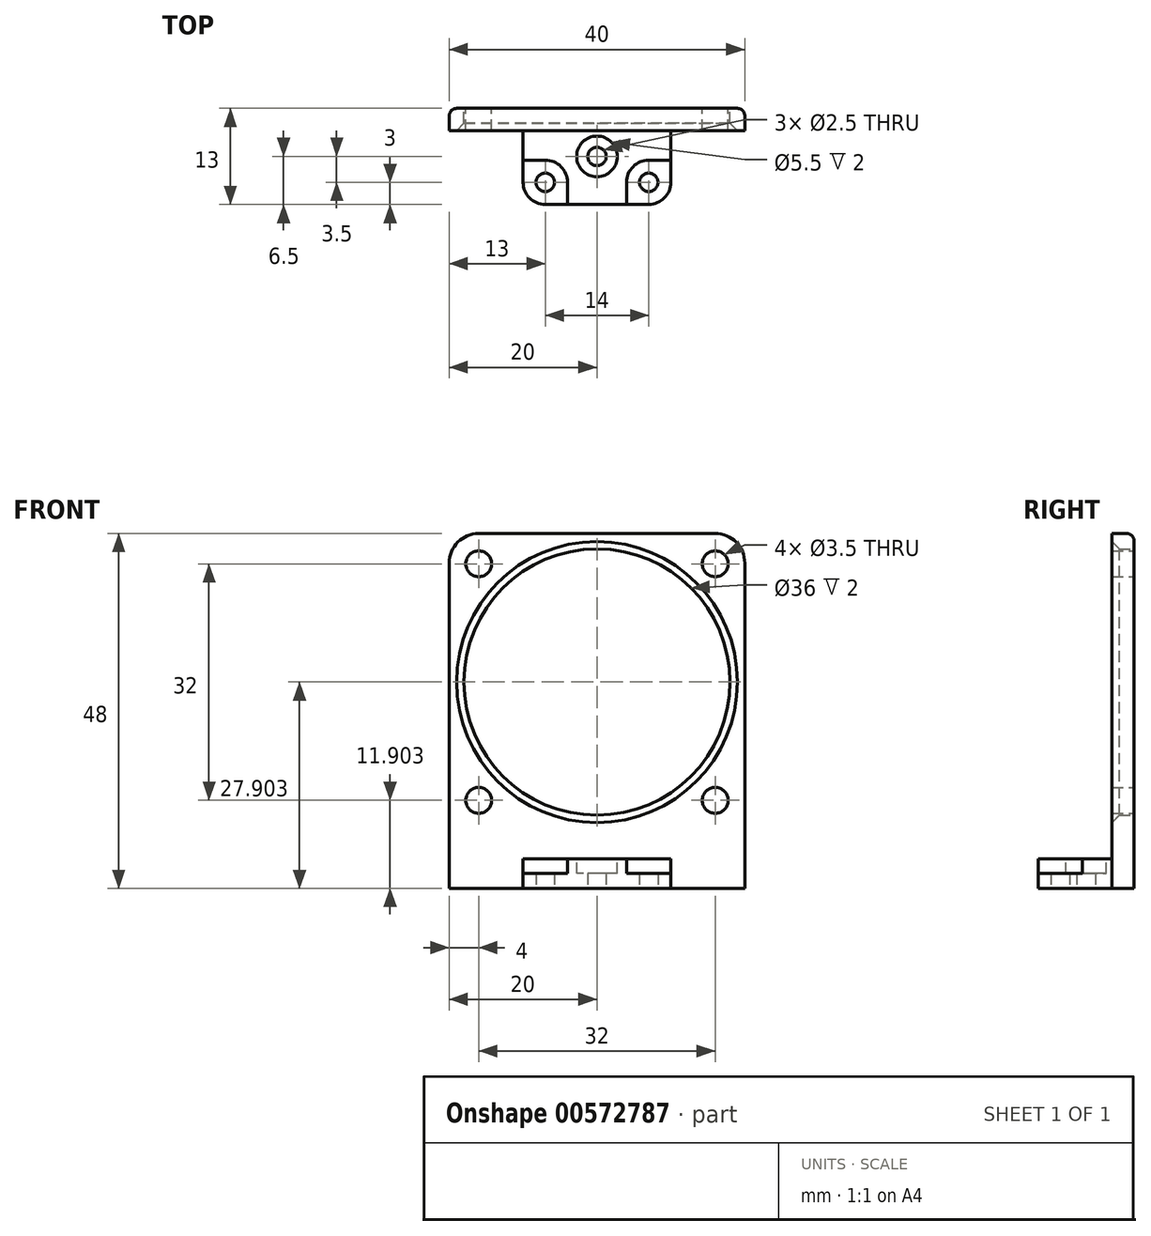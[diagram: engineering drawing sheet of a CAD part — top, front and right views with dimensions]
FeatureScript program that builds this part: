
annotation { "Feature Type Name" : "Feature", "Feature Type Description" : "" }
export const myFeature = defineFeature(function(context is Context, id is Id, definition is map)
    precondition{}
    {
        {
            var Q0;
            Q0=qCreatedBy(makeId("Front.planeOp"),FACE);
            var sketch = newSketch(context, id + "F0", { "sketchPlane" : qUnion([Q0])});
            skLineSegment(sketch, "E0.bottom", {"start": v(-20, 48) * mm, "end": v(20, 48) * mm});
            skLineSegment(sketch, "E0.top", {"start": v(-20, 0) * mm, "end": v(20, 0) * mm});
            skLineSegment(sketch, "E0.left", {"start": v(-20, 48) * mm, "end": v(-20, 0) * mm});
            skLineSegment(sketch, "E0.right", {"start": v(20, 48) * mm, "end": v(20, 0) * mm});
            skCircle(sketch, "E1", {"center": v(0, 27.9) * mm, "radius": 18 * mm});
            skCircle(sketch, "E2", {"center": v(-16, 43.9) * mm, "radius": 1.75 * mm});
            skCircle(sketch, "E3", {"center": v(16, 43.9) * mm, "radius": 1.75 * mm});
            skCircle(sketch, "E4", {"center": v(-16, 11.9) * mm, "radius": 1.75 * mm});
            skCircle(sketch, "E5", {"center": v(16, 11.9) * mm, "radius": 1.75 * mm});
            skSolve(sketch);
        }
        {
            var Q0;
            Q0 = qSketchRegion(id + "F0", true);
            extrude(context, id + "F1", {"entities" : qUnion([Q0]), "depth" : 3 * mm, "offsetDistance" : 25 * mm});
        }
        {
            var Q0;
            Q0=qCreatedBy(makeId("Front.planeOp"),FACE);
            var sketch = newSketch(context, id + "F2", { "sketchPlane" : qUnion([Q0])});
            skLineSegment(sketch, "E6.bottom", {"start": v(-10, 4) * mm, "end": v(10, 4) * mm});
            skLineSegment(sketch, "E6.top", {"start": v(-10, 0) * mm, "end": v(10, 0) * mm});
            skLineSegment(sketch, "E6.left", {"start": v(-10, 4) * mm, "end": v(-10, 0) * mm});
            skLineSegment(sketch, "E6.right", {"start": v(10, 4) * mm, "end": v(10, 0) * mm});
            skSolve(sketch);
        }
        {
            var Q0;
            Q0 = qSketchRegion(id + "F2", true);
            extrude(context, id + "F3", {"entities" : qUnion([Q0]), "operationType" : NewBodyOperationType.ADD, "depth" : 13 * mm, "offsetDistance" : 25 * mm});
        }
        {
            var Q0;
            Q0=qCreatedBy(makeId("Top.planeOp"),FACE);
            var sketch = newSketch(context, id + "F4", { "sketchPlane" : qUnion([Q0])});
            skCircle(sketch, "E7", {"center": v(0, -6.5) * mm, "radius": 1.25 * mm});
            skCircle(sketch, "E8", {"center": v(-7, -10) * mm, "radius": 1.25 * mm});
            skCircle(sketch, "E9", {"center": v(7, -10) * mm, "radius": 1.25 * mm});
            skSolve(sketch);
        }
        {
            var Q0;
            Q0 = qSketchRegion(id + "F4", true);
            extrude(context, id + "F5", {"entities" : qUnion([Q0]), "operationType" : NewBodyOperationType.REMOVE, "depth" : 25 * mm, "offsetDistance" : 25 * mm});
        }
        {
            var Q0;
            Q0=makeQuery(id+"F3.opExtrude","SWEPT_FACE",FACE,{"disambiguationData":[OSD([sQuery(id+"F2.wireOp",EDGE,"E6.bottom")])]});
            var sketch = newSketch(context, id + "F6", { "sketchPlane" : qUnion([Q0])});
            skLineSegment(sketch, "E10.bottom", {"start": v(-10, -13) * mm, "end": v(-4, -13) * mm});
            skLineSegment(sketch, "E10.top", {"start": v(-10, -7) * mm, "end": v(-4, -7) * mm});
            skLineSegment(sketch, "E10.left", {"start": v(-10, -13) * mm, "end": v(-10, -7) * mm});
            skLineSegment(sketch, "E10.right", {"start": v(-4, -13) * mm, "end": v(-4, -7) * mm});
            skLineSegment(sketch, "E11.bottom", {"start": v(10, -13) * mm, "end": v(4, -13) * mm});
            skLineSegment(sketch, "E11.top", {"start": v(10, -7) * mm, "end": v(4, -7) * mm});
            skLineSegment(sketch, "E11.left", {"start": v(10, -13) * mm, "end": v(10, -7) * mm});
            skLineSegment(sketch, "E11.right", {"start": v(4, -13) * mm, "end": v(4, -7) * mm});
            skCircle(sketch, "E12", {"center": v(0, -6.5) * mm, "radius": 2.75 * mm});
            skSolve(sketch);
        }
        {
            var Q0;
            Q0 = qSketchRegion(id + "F6", true);
            extrude(context, id + "F7", {"entities" : qUnion([Q0]), "operationType" : NewBodyOperationType.REMOVE, "oppositeDirection" : true, "depth" : 2 * mm, "offsetDistance" : 25 * mm});
        }
        {
            var Q0;
            Q0=makeQuery(id+"F1.opExtrude","SWEPT_EDGE",EDGE,{"disambiguationData":[OSD([sQuery(id+"F0.wireOp",EDGE,"E0.bottom"),sQuery(id+"F0.wireOp",EDGE,"E0.right")])]});
            var Q1;
            Q1=makeQuery(id+"F1.opExtrude","SWEPT_EDGE",EDGE,{"disambiguationData":[OSD([sQuery(id+"F0.wireOp",EDGE,"E0.bottom"),sQuery(id+"F0.wireOp",EDGE,"E0.left")])]});
            fillet(context, id + "F8", {"entities" : qUnion([Q0, Q1]), "radius" : 4 * mm, "tangentPropagation" : true, "allowEdgeOverflow" : false});
        }
        {
            var Q0;
            Q0=makeQuery(id+"F7.boolean.opBoolean","COPY",EDGE,{"derivedFrom":makeQuery(id+"F7.opExtrude","SWEPT_EDGE",EDGE,{"disambiguationData":[OSD([sQuery(id+"F6.wireOp",EDGE,"E11.top"),sQuery(id+"F6.wireOp",EDGE,"E11.right")])]})});
            var Q1;
            Q1=makeQuery(id+"F3.opExtrude","CAP_EDGE",EDGE,{"disambiguationData":[OSD([sQuery(id+"F2.wireOp",EDGE,"E6.right")])],"isStart":false});
            var Q2;
            Q2=makeQuery(id+"F7.boolean.opBoolean","COPY",EDGE,{"derivedFrom":makeQuery(id+"F7.opExtrude","SWEPT_EDGE",EDGE,{"disambiguationData":[OSD([sQuery(id+"F6.wireOp",EDGE,"E10.top"),sQuery(id+"F6.wireOp",EDGE,"E10.right")])]})});
            var Q3;
            Q3=makeQuery(id+"F3.opExtrude","CAP_EDGE",EDGE,{"disambiguationData":[OSD([sQuery(id+"F2.wireOp",EDGE,"E6.left")])],"isStart":false});
            fillet(context, id + "F9", {"entities" : qUnion([Q0, Q1, Q2, Q3]), "radius" : 3 * mm, "tangentPropagation" : true, "allowEdgeOverflow" : false});
        }
        {
            var Q0;
            Q0=makeQuery(id+"F1.opExtrude","CAP_EDGE",EDGE,{"disambiguationData":[OSD([sQuery(id+"F0.wireOp",EDGE,"E1")])],"isStart":false});
            chamfer(context, id + "F10", {"entities" : qUnion([Q0]), "width" : 1 * mm, "tangentPropagation" : true});
        }
        {
            var Q0;
            Q0=makeQuery(id+"F1.opExtrude","CAP_EDGE",EDGE,{"disambiguationData":[OSD([sQuery(id+"F0.wireOp",EDGE,"E0.right")])],"isStart":true});
            fillet(context, id + "F11", {"entities" : qUnion([Q0]), "radius" : 1 * mm, "tangentPropagation" : true, "allowEdgeOverflow" : false});
        }
    });
